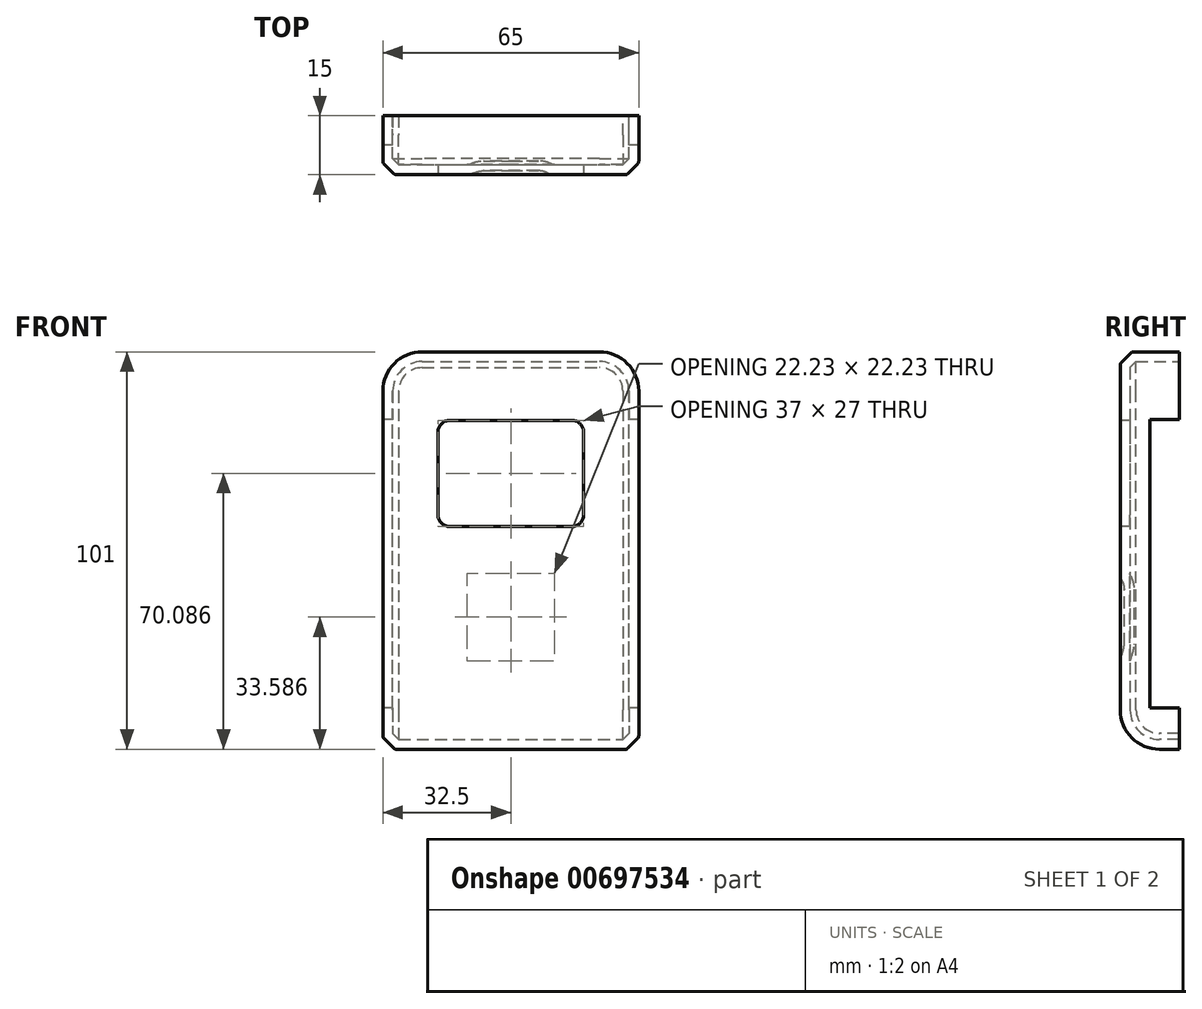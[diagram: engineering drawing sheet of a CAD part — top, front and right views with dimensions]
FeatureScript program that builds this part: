
annotation { "Feature Type Name" : "Feature", "Feature Type Description" : "" }
export const myFeature = defineFeature(function(context is Context, id is Id, definition is map)
    precondition{}
    {
        {
            var Q0;
            Q0=qCreatedBy(makeId("Front.planeOp"),FACE);
            var sketch = newSketch(context, id + "F0", { "sketchPlane" : qUnion([Q0])});
            skLineSegment(sketch, "E0.bottom", {"start": v(-22.5, 50.5) * mm, "end": v(22.5, 50.5) * mm});
            skLineSegment(sketch, "E0.top", {"start": v(-32.5, -50.5) * mm, "end": v(32.5, -50.5) * mm});
            skLineSegment(sketch, "E0.left", {"start": v(-32.5, 40.5) * mm, "end": v(-32.5, -50.5) * mm});
            skLineSegment(sketch, "E0.right", {"start": v(32.5, 40.5) * mm, "end": v(32.5, -50.5) * mm});
            skPoint(sketch, "E0.middle", {"position": v(0, 0) * mm});
            skPoint(sketch, "E1.visualSharp", {"position": v(-32.5, 50.5) * mm});
            skArc(sketch, "E1.filletArc", {"start": v(-22.5, 50.5) * mm, "mid": v(-29.57, 47.57) * mm, "end": v(-32.5, 40.5) * mm});
            skPoint(sketch, "E2.visualSharp", {"position": v(32.5, 50.5) * mm});
            skArc(sketch, "E2.filletArc", {"start": v(32.5, 40.5) * mm, "mid": v(29.57, 47.57) * mm, "end": v(22.5, 50.5) * mm});
            skSolve(sketch);
        }
        {
            var Q0;
            Q0 = qSketchRegion(id + "F0", true);
            extrude(context, id + "F1", {"entities" : qUnion([Q0]), "depth" : 15 * mm, "offsetDistance" : 25.4 * mm});
        }
        {
            var Q0;
            Q0=makeQuery(id+"F1.opExtrude","CAP_EDGE",EDGE,{"disambiguationData":[OSD([sQuery(id+"F0.wireOp",EDGE,"E0.top")])],"isStart":false});
            fillet(context, id + "F2", {"entities" : qUnion([Q0]), "radius" : 10 * mm, "tangentPropagation" : true, "allowEdgeOverflow" : false});
        }
        {
            var Q0;
            Q0=makeQuery(id+"F1.opExtrude","CAP_EDGE",EDGE,{"disambiguationData":[OSD([sQuery(id+"F0.wireOp",EDGE,"E0.right")])],"isStart":false});
            chamfer(context, id + "F3", {"entities" : qUnion([Q0]), "width" : 3 * mm, "tangentPropagation" : true});
        }
        {
            var Q0;
            {var subQ0=sQuery(id+"F0.wireOp",EDGE,"E0.right");Q0=makeQuery(id+"F3.opChamfer","BLEND_EDGE",EDGE,{"blendedFrom":[makeQuery(id+"F1.opExtrude","CAP_EDGE",EDGE,{"disambiguationData":[OSD([subQ0])],"isStart":false}),makeQuery(id+"F1.opExtrude","SWEPT_FACE",FACE,{"disambiguationData":[OSD([subQ0])]})],"blendedInto":[makeQuery(id+"F1.opExtrude","SWEPT_FACE",FACE,{"disambiguationData":[OSD([subQ0])]})]});}
            var Q1;
            {var subQ0=sQuery(id+"F0.wireOp",EDGE,"E0.left");Q1=makeQuery(id+"F3.opChamfer","BLEND_EDGE",EDGE,{"blendedFrom":[makeQuery(id+"F1.opExtrude","CAP_EDGE",EDGE,{"disambiguationData":[OSD([subQ0])],"isStart":false}),makeQuery(id+"F1.opExtrude","SWEPT_FACE",FACE,{"disambiguationData":[OSD([subQ0])]})],"blendedInto":[makeQuery(id+"F1.opExtrude","SWEPT_FACE",FACE,{"disambiguationData":[OSD([subQ0])]})]});}
            var Q2;
            {var subQ0=sQuery(id+"F0.wireOp",EDGE,"E0.right");Q2=makeQuery(id+"F3.opChamfer","BLEND_EDGE",EDGE,{"blendedFrom":[makeQuery(id+"F1.opExtrude","CAP_EDGE",EDGE,{"disambiguationData":[OSD([subQ0])],"isStart":false}),makeQuery(id+"F1.opExtrude","CAP_FACE",FACE,{"disambiguationData":[OSD([sQuery(id+"F0.wireOp",EDGE,"E0.bottom"),sQuery(id+"F0.wireOp",EDGE,"E0.top"),sQuery(id+"F0.wireOp",EDGE,"E0.left"),subQ0,sQuery(id+"F0.wireOp",EDGE,"E1.filletArc"),sQuery(id+"F0.wireOp",EDGE,"E2.filletArc")])],"isStart":false})],"blendedInto":[makeQuery(id+"F1.opExtrude","CAP_FACE",FACE,{"disambiguationData":[OSD([sQuery(id+"F0.wireOp",EDGE,"E0.bottom"),sQuery(id+"F0.wireOp",EDGE,"E0.top"),sQuery(id+"F0.wireOp",EDGE,"E0.left"),subQ0,sQuery(id+"F0.wireOp",EDGE,"E1.filletArc"),sQuery(id+"F0.wireOp",EDGE,"E2.filletArc")])],"isStart":false})]});}
            fillet(context, id + "F4", {"entities" : qUnion([Q0, Q1, Q2]), "radius" : 1 * mm, "tangentPropagation" : true, "allowEdgeOverflow" : false});
        }
        {
            var Q0;
            Q0=makeQuery(id+"F1.opExtrude","CAP_FACE",FACE,{"disambiguationData":[OSD([sQuery(id+"F0.wireOp",EDGE,"E0.bottom"),sQuery(id+"F0.wireOp",EDGE,"E0.top"),sQuery(id+"F0.wireOp",EDGE,"E0.left"),sQuery(id+"F0.wireOp",EDGE,"E0.right"),sQuery(id+"F0.wireOp",EDGE,"E1.filletArc"),sQuery(id+"F0.wireOp",EDGE,"E2.filletArc")])],"isStart":false});
            var sketch = newSketch(context, id + "F5", { "sketchPlane" : qUnion([Q0])});
            skLineSegment(sketch, "E3.bottom", {"start": v(-15.5, 33.09) * mm, "end": v(15.5, 33.09) * mm});
            skLineSegment(sketch, "E3.top", {"start": v(-15.5, 6.09) * mm, "end": v(15.5, 6.09) * mm});
            skLineSegment(sketch, "E3.left", {"start": v(-18.5, 30.09) * mm, "end": v(-18.5, 9.09) * mm});
            skLineSegment(sketch, "E3.right", {"start": v(18.5, 30.09) * mm, "end": v(18.5, 9.09) * mm});
            skPoint(sketch, "E3.middle", {"position": v(0, 19.59) * mm});
            skPoint(sketch, "E4.visualSharp", {"position": v(-18.5, 33.09) * mm});
            skArc(sketch, "E4.filletArc", {"start": v(-15.5, 33.09) * mm, "mid": v(-17.62, 32.2) * mm, "end": v(-18.5, 30.09) * mm});
            skPoint(sketch, "E5.visualSharp", {"position": v(18.5, 33.09) * mm});
            skArc(sketch, "E5.filletArc", {"start": v(18.5, 30.09) * mm, "mid": v(17.62, 32.2) * mm, "end": v(15.5, 33.09) * mm});
            skPoint(sketch, "E6.visualSharp", {"position": v(18.5, 6.09) * mm});
            skArc(sketch, "E6.filletArc", {"start": v(15.5, 6.09) * mm, "mid": v(17.62, 6.96) * mm, "end": v(18.5, 9.09) * mm});
            skPoint(sketch, "E7.visualSharp", {"position": v(-18.5, 6.09) * mm});
            skArc(sketch, "E7.filletArc", {"start": v(-18.5, 9.09) * mm, "mid": v(-17.62, 6.96) * mm, "end": v(-15.5, 6.09) * mm});
            skSolve(sketch);
        }
        {
            var Q0;
            Q0=makeQuery(id+"F5.imprint","IMPRINT",FACE,{"disambiguationData":[TD([[makeQuery(id+"F5.imprint","IMPRINT",EDGE,{"derivedFrom":sQuery(id+"F5.wireOp",EDGE,"E3.bottom")}),-1.0]])]});
            extrude(context, id + "F6", {"entities" : qUnion([Q0]), "operationType" : NewBodyOperationType.REMOVE, "oppositeDirection" : true, "depth" : 25.4 * mm, "offsetDistance" : 25.4 * mm});
        }
        {
            var Q0;
            Q0=makeQuery(id+"F1.opExtrude","CAP_FACE",FACE,{"disambiguationData":[OSD([sQuery(id+"F0.wireOp",EDGE,"E0.bottom"),sQuery(id+"F0.wireOp",EDGE,"E0.top"),sQuery(id+"F0.wireOp",EDGE,"E0.left"),sQuery(id+"F0.wireOp",EDGE,"E0.right"),sQuery(id+"F0.wireOp",EDGE,"E1.filletArc"),sQuery(id+"F0.wireOp",EDGE,"E2.filletArc")])],"isStart":false});
            var sketch = newSketch(context, id + "F7", { "sketchPlane" : qUnion([Q0])});
            skCircle(sketch, "E8", {"center": v(0, -16.91) * mm, "radius": 10 * mm});
            skSolve(sketch);
        }
        {
            var Q0;
            Q0 = qSketchRegion(id + "F7", true);
            extrude(context, id + "F8", {"entities" : qUnion([Q0]), "operationType" : NewBodyOperationType.REMOVE, "oppositeDirection" : true, "depth" : 1 * mm, "offsetDistance" : 25.4 * mm});
        }
        {
            var Q0;
            Q0=makeQuery(id+"F8.boolean.opBoolean","COPY",EDGE,{"derivedFrom":makeQuery(id+"F8.opExtrude","CAP_EDGE",EDGE,{"disambiguationData":[OSD([sQuery(id+"F7.wireOp",EDGE,"E8")])],"isStart":false})});
            fillet(context, id + "F9", {"entities" : qUnion([Q0]), "radius" : 5.08 * mm, "tangentPropagation" : true, "allowEdgeOverflow" : false});
        }
        {
            var Q0;
            Q0=makeQuery(id+"F9.opFillet","BLEND_EDGE",EDGE,{"blendedFrom":[makeQuery(id+"F8.boolean.opBoolean","COPY",EDGE,{"derivedFrom":makeQuery(id+"F8.opExtrude","CAP_EDGE",EDGE,{"disambiguationData":[OSD([sQuery(id+"F7.wireOp",EDGE,"E8")])],"isStart":false})}),makeQuery(id+"F1.opExtrude","CAP_FACE",FACE,{"disambiguationData":[OSD([sQuery(id+"F0.wireOp",EDGE,"E0.bottom"),sQuery(id+"F0.wireOp",EDGE,"E0.top"),sQuery(id+"F0.wireOp",EDGE,"E0.left"),sQuery(id+"F0.wireOp",EDGE,"E0.right"),sQuery(id+"F0.wireOp",EDGE,"E1.filletArc"),sQuery(id+"F0.wireOp",EDGE,"E2.filletArc")])],"isStart":false})],"blendedInto":[makeQuery(id+"F1.opExtrude","CAP_FACE",FACE,{"disambiguationData":[OSD([sQuery(id+"F0.wireOp",EDGE,"E0.bottom"),sQuery(id+"F0.wireOp",EDGE,"E0.top"),sQuery(id+"F0.wireOp",EDGE,"E0.left"),sQuery(id+"F0.wireOp",EDGE,"E0.right"),sQuery(id+"F0.wireOp",EDGE,"E1.filletArc"),sQuery(id+"F0.wireOp",EDGE,"E2.filletArc")])],"isStart":false})]});
            fillet(context, id + "F10", {"entities" : qUnion([Q0]), "radius" : 4 * mm, "tangentPropagation" : true, "rho" : 0.5, "crossSection" : FilletCrossSection.CONIC, "allowEdgeOverflow" : false});
        }
        {
            var Q0;
            Q0=makeQuery(id+"F6.boolean.opBoolean","COPY",FACE,{"derivedFrom":makeQuery(id+"F6.opExtrude","SWEPT_FACE",FACE,{"disambiguationData":[OSD([sQuery(id+"F5.wireOp",EDGE,"E3.right")])]})});
            var Q1;
            Q1=makeQuery(id+"F6.boolean.opBoolean","COPY",FACE,{"derivedFrom":makeQuery(id+"F6.opExtrude","SWEPT_FACE",FACE,{"disambiguationData":[OSD([sQuery(id+"F5.wireOp",EDGE,"E5.filletArc")])]})});
            var Q2;
            Q2=makeQuery(id+"F6.boolean.opBoolean","COPY",FACE,{"derivedFrom":makeQuery(id+"F6.opExtrude","SWEPT_FACE",FACE,{"disambiguationData":[OSD([sQuery(id+"F5.wireOp",EDGE,"E3.bottom")])]})});
            var Q3;
            Q3=makeQuery(id+"F6.boolean.opBoolean","COPY",FACE,{"derivedFrom":makeQuery(id+"F6.opExtrude","SWEPT_FACE",FACE,{"disambiguationData":[OSD([sQuery(id+"F5.wireOp",EDGE,"E4.filletArc")])]})});
            var Q4;
            Q4=makeQuery(id+"F6.boolean.opBoolean","COPY",FACE,{"derivedFrom":makeQuery(id+"F6.opExtrude","SWEPT_FACE",FACE,{"disambiguationData":[OSD([sQuery(id+"F5.wireOp",EDGE,"E3.left")])]})});
            var Q5;
            Q5=makeQuery(id+"F6.boolean.opBoolean","COPY",FACE,{"derivedFrom":makeQuery(id+"F6.opExtrude","SWEPT_FACE",FACE,{"disambiguationData":[OSD([sQuery(id+"F5.wireOp",EDGE,"E7.filletArc")])]})});
            var Q6;
            Q6=makeQuery(id+"F6.boolean.opBoolean","COPY",FACE,{"derivedFrom":makeQuery(id+"F6.opExtrude","SWEPT_FACE",FACE,{"disambiguationData":[OSD([sQuery(id+"F5.wireOp",EDGE,"E3.top")])]})});
            var Q7;
            Q7=makeQuery(id+"F6.boolean.opBoolean","COPY",FACE,{"derivedFrom":makeQuery(id+"F6.opExtrude","SWEPT_FACE",FACE,{"disambiguationData":[OSD([sQuery(id+"F5.wireOp",EDGE,"E6.filletArc")])]})});
            var Q8;
            Q8=makeQuery(id+"F1.opExtrude","CAP_FACE",FACE,{"disambiguationData":[OSD([sQuery(id+"F0.wireOp",EDGE,"E0.bottom"),sQuery(id+"F0.wireOp",EDGE,"E0.top"),sQuery(id+"F0.wireOp",EDGE,"E0.left"),sQuery(id+"F0.wireOp",EDGE,"E0.right"),sQuery(id+"F0.wireOp",EDGE,"E1.filletArc"),sQuery(id+"F0.wireOp",EDGE,"E2.filletArc")])],"isStart":true});
            shell(context, id + "F11", {"entities" : qUnion([Q0, Q1, Q2, Q3, Q4, Q5, Q6, Q7, Q8]), "thickness" : 2.5 * mm});
        }
        {
            var Q0;
            Q0=makeQuery(id+"F1.opExtrude","SWEPT_FACE",FACE,{"disambiguationData":[OSD([sQuery(id+"F0.wireOp",EDGE,"E0.left")])]});
            var sketch = newSketch(context, id + "F12", { "sketchPlane" : qUnion([Q0])});
            skLineSegment(sketch, "E9.bottom", {"start": v(0, 33.26) * mm, "end": v(7.45, 33.26) * mm});
            skLineSegment(sketch, "E9.top", {"start": v(0, -39.95) * mm, "end": v(7.45, -39.95) * mm});
            skLineSegment(sketch, "E9.left", {"start": v(0, 33.26) * mm, "end": v(0, -39.95) * mm});
            skLineSegment(sketch, "E9.right", {"start": v(7.45, 33.26) * mm, "end": v(7.45, -39.95) * mm});
            skSolve(sketch);
        }
        {
            var Q0;
            Q0 = qSketchRegion(id + "F12", true);
            var Q1;
            Q1=makeQuery(id+"F3.opChamfer","BLEND_FACE",FACE,{"disambiguationData":[OSD([sQuery(id+"F0.wireOp",EDGE,"E0.right")])]});
            extrude(context, id + "F13", {"entities" : qUnion([Q0, Q1]), "operationType" : NewBodyOperationType.REMOVE, "oppositeDirection" : true, "depth" : 81.8 * mm, "offsetDistance" : 25 * mm});
        }
    });
